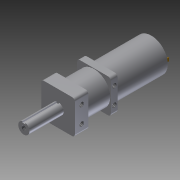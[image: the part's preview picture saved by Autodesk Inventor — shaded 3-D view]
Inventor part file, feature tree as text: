
AUTODESK INVENTOR PART (.ipt)
format: ipt  version: 2011 (Build 150239000, 239)  size: 203,264 bytes
history: native  units: in
note: dims shown in document units (in); Inventor stores cm internally (conversion verified against a paired STEP export)
features: sketch x10, extrude x8, fillet x3, hole x2, projected_geometry x2, plane x1, mirror x1
ambient origin geometry x8: Origin, YZ Plane, XZ Plane, XY Plane, X Axis, Y Axis, Z Axis, Center Point
bodies: Solid3 (feature_tree)
feature tree (27):
  extrude  "Extrusion2"  Depth=1.5in
  extrude  "Extrusion3"  Depth=1.45in
  extrude  "Extrusion4"  Depth=0.6in TaperAngle=0.0deg
  extrude  "Extrusion5"  Depth=0.125in
  hole  "Hole1"  [1 undecoded]
  plane  "Work Plane1"
  mirror  "Mirror1"
  hole  "Hole2"  [1 undecoded]
  extrude  "Extrusion6"  Depth=1.47in
  extrude  "Extrusion7"  Depth=0.15in
  extrude  "Extrusion8"  Depth=0.55in
  extrude  "Extrusion9"  Depth=0.55in
  fillet  "Fillet1"  Radius=0.215in
  fillet  "Fillet2"  Radius=0.5in
  fillet  "Fillet3"  Radius=0.16in
  sketch  "Sketch3"  dims[d4=1.5in d5=1.5in]
  sketch  "Sketch4"  dims[d6=0.3in d7=0.0in d8=1.45in]
  sketch  "Sketch5"  dims[d9=1.0in d10=0.0in d11=0.6in d12=0.0in]
  projected_geometry  "Projected Loop1"
  sketch  "Sketch6"  dims[d13=0.5in d14=0.125in]
  sketch  "Sketch7"  dims[d16=0.0625in d17=1.52in d18=0.0in]
  projected_geometry  "Projected Loop2"
  sketch  "Sketch8"  dims[d19=0.375in d20=0.375in]
  sketch  "Sketch9"  dims[d21=0.196in d22=0.3in d23=0.375in d24=0.25in d25=0.5635in d26=1.0in d27=0.8108in]
  sketch  "Sketch10"  dims[d28=0.196in d29=0.3in d30=0.375in d31=0.25in d32=0.5635in d33=1.0in d34=0.8108in d35=1.47in]
  sketch  "Sketch11"  dims[d36=2.25in d37=0.0in d38=0.15in]
  sketch  "Sketch12"  dims[d39=0.025in d40=0.55in d41=0.55in d42=0.215in d43=0.0in d44=0.5in d45=0.16in d46=0.0in d47=0.126in d48=0.05in d49=0.0in d50=0.0625in d51=0.0312in d52=0.125in]
note: 2 required parameter values undecoded (feature->parameter linkage not recoverable at this tier; creation-order binding heuristic only, values carry confidence <= 0.55)
